# Revit family: 28L 2 to 6 units single sided indoor manifold system rev
name_source: partatom
category: Plumbing Fixtures
revit_build: Autodesk Revit 2017 (Build: 20160225_1515(x64)
units: mm (PartAtom-declared; Revit-internal decimal feet)

## family parameters
Always vertical = Yes
Cut with Voids When Loaded = No
Part Type = Normal
Room Calculation Point = No
Round Connector Dimension = Use Diameter
Shared = No
Work Plane-Based = No

## types (10) — shared parameters
Cold Water Inlet Pipe connector description = Male threaded connector R1-1/2"
Cold Water Inlet Pipe diameter = 38.1mm(DN 40)
Exhaust Air pipe connector description = 80-125mm coaxial air connector
Exhaust Air pipe connector system classification = Exhaust Air
Exhaust Air pipe diameter = 125.000 mm
Gas Inlet Pipe connector description = Male threaded connector R1-1/2"
Gas Inlet Pipe diameter = 38.1mm(DN 40)
Hot Water Outlet Pipe connector description = Male threaded connector R1-1/2"
Hot Water Outlet Pipe diameter = 38.1mm(DN 40)
Supply Air/Air Inlet connector classification = Supply Air
Supply Air/Air Inlet pipe connector description = 80-125mm coaxial air connector
Supply Air/Air Inlet pipe diameter = 80.000 mm

## per-type parameters (varying)
- 28L 2 units single sided indoor floor mounted: 2 Unit L=Yes; 2 Unit R=No; 3 Unit L=No; 3 Unit R=No; Array Offset=360.000 mm; Base Offset L=794.000 mm; Base Offset R=1040.000 mm; Base Support L=Yes; Base Support R=No; Connector Left=2324.000 mm; Connector Right=1550.000 mm; D1=1757.000 mm; D2=217.000 mm; D3=1757.000 mm; No of Connectors 1=2; No of Connectors 2=2; No. of power supply point required=2; Nominal depth=900mm; Nominal height=1540mm; Nominal width=794mm; Number of Gas Water Heaters=2; Product SKU Dux brand=D22800FN/LFx; Product SKU Thermann brand=T22800FN/LFx; Product description=Gas Water heater Manifold 2 unit indoor floor mounted; Total Max. power requirement=386W; Total nominal gas consumption (MJ/h)=410; Total number of exhaust air connections=2; Total number of supply air connections=2; Unit Offset=41.300 mm; Weight (Kg)=90
- 28L 3 units single sided indoor floor mounted: 2 Unit L=No; 2 Unit R=No; 3 Unit L=Yes; 3 Unit R=No; Array Offset=360.000 mm; Base Offset L=1170.000 mm; Base Offset R=1040.000 mm; Base Support L=Yes; Base Support R=No; Connector Left=2700.000 mm; Connector Right=1550.000 mm; D1=2125.000 mm; D2=225.000 mm; D3=1765.000 mm; No of Connectors 1=3; No of Connectors 2=3; No. of power supply point required=3; Nominal depth=900mm; Nominal height=1540mm; Nominal width=1170mm; Number of Gas Water Heaters=3; Product SKU Dux brand=D32800FN/LFx; Product SKU Thermann brand=T32800FN/LFx; Product description=Gas Water heater Manifold 3 unit indoor floor mounted; Total Max. power requirement=579W; Total nominal gas consumption (MJ/h)=615; Total number of exhaust air connections=3; Total number of supply air connections=3; Unit Offset=41.300 mm; Weight (Kg)=120
- 28L 4 units single sided indoor floor mounted: 2 Unit L=Yes; 2 Unit R=Yes; 3 Unit L=No; 3 Unit R=No; Array Offset=360.000 mm; Base Offset L=794.000 mm; Base Offset R=794.000 mm; Base Support L=Yes; Base Support R=Yes; Connector Left=2324.000 mm; Connector Right=756.000 mm; D1=963.000 mm; D2=217.000 mm; D3=963.000 mm; No of Connectors 1=2; No of Connectors 2=2; No. of power supply point required=4; Nominal depth=900mm; Nominal height=1540mm; Nominal width=1588mm; Number of Gas Water Heaters=4; Product SKU Dux brand=D42800FN/LFx; Product SKU Thermann brand=T42800FN/LFx; Product description=Gas Water heater Manifold 4 unit indoor floor mounted; Total Max. power requirement=772W; Total nominal gas consumption (MJ/h)=820; Total number of exhaust air connections=4; Total number of supply air connections=4; Unit Offset=41.300 mm; Weight (Kg)=180
- 28L 5 units single sided indoor floor mounted: 2 Unit L=No; 2 Unit R=Yes; 3 Unit L=Yes; 3 Unit R=No; Array Offset=360.000 mm; Base Offset L=1170.000 mm; Base Offset R=794.000 mm; Base Support L=Yes; Base Support R=Yes; Connector Left=2700.000 mm; Connector Right=756.000 mm; D1=2125.000 mm; D2=225.000 mm; D3=963.000 mm; No of Connectors 1=2; No of Connectors 2=3; No. of power supply point required=5; Nominal depth=900mm; Nominal height=1540mm; Nominal width=1964mm; Number of Gas Water Heaters=5; Product SKU Dux brand=D52800FN/LFx; Product SKU Thermann brand=T52800FN/LFx; Product description=Gas Water heater Manifold 5 unit indoor floor mounted; Total Max. power requirement=965W; Total nominal gas consumption (MJ/h)=1025; Total number of exhaust air connections=5; Total number of supply air connections=5; Unit Offset=41.300 mm; Weight (Kg)=210
- 28L 6 units single sided indoor floor mounted: 2 Unit L=No; 2 Unit R=No; 3 Unit L=Yes; 3 Unit R=Yes; Array Offset=1170.000 mm; Base Offset L=1170.000 mm; Base Offset R=1170.000 mm; Base Support L=Yes; Base Support R=Yes; Connector Left=2700.000 mm; Connector Right=380.000 mm; D1=1315.000 mm; D2=225.000 mm; D3=595.000 mm; No of Connectors 1=3; No of Connectors 2=3; No. of power supply point required=6; Nominal depth=900mm; Nominal height=1540mm; Nominal width=2340mm; Number of Gas Water Heaters=6; Product SKU Dux brand=D62800FN/LFx; Product SKU Thermann brand=T62800FN/LFx; Product description=Gas Water heater Manifold 6 unit  indoor floor mounted; Total Max. power requirement=1158W; Total nominal gas consumption (MJ/h)=1230; Total number of exhaust air connections=6; Total number of supply air connections=6; Unit Offset=41.300 mm; Weight (Kg)=240
- 28L 2 units single sided indoor wall mounted: 2 Unit L=Yes; 2 Unit R=No; 3 Unit L=No; 3 Unit R=No; Array Offset=360.000 mm; Base Offset L=1040.000 mm; Base Offset R=1040.000 mm; Base Support L=No; Base Support R=No; Connector Left=2324.000 mm; Connector Right=1550.000 mm; D1=1757.000 mm; D2=217.000 mm; D3=1757.000 mm; No of Connectors 1=2; No of Connectors 2=2; No. of power supply point required=2; Nominal depth=332mm; Nominal height=1500mm; Nominal width=794mm; Number of Gas Water Heaters=2; Product SKU Dux brand=D22800FN/LWx; Product SKU Thermann brand=T22800FN/LWx; Product description=Gas Water heater Manifold 2 unit indoor wall mounted; Total Max. power requirement=386W; Total nominal gas consumption (MJ/h)=410; Total number of exhaust air connections=2; Total number of supply air connections=2; Unit Offset=0.000 mm; Weight (Kg)=90
- 28L 3 units single sided indoor wall mounted: 2 Unit L=No; 2 Unit R=No; 3 Unit L=Yes; 3 Unit R=No; Array Offset=360.000 mm; Base Offset L=1540.000 mm; Base Offset R=1040.000 mm; Base Support L=No; Base Support R=No; Connector Left=2700.000 mm; Connector Right=1550.000 mm; D1=2125.000 mm; D2=225.000 mm; D3=1765.000 mm; No of Connectors 1=3; No of Connectors 2=3; No. of power supply point required=3; Nominal depth=332mm; Nominal height=1500mm; Nominal width=1170mm; Number of Gas Water Heaters=3; Product SKU Dux brand=D32800FN/LWx; Product SKU Thermann brand=T32800FN/LWx; Product description=Gas Water heater Manifold 3 unit indoor wall mounted; Total Max. power requirement=579W; Total nominal gas consumption (MJ/h)=615; Total number of exhaust air connections=3; Total number of supply air connections=3; Unit Offset=0.000 mm; Weight (Kg)=120
- 28L 4 units single sided indoor wall mounted: 2 Unit L=Yes; 2 Unit R=Yes; 3 Unit L=No; 3 Unit R=No; Array Offset=360.000 mm; Base Offset L=1040.000 mm; Base Offset R=1040.000 mm; Base Support L=No; Base Support R=No; Connector Left=2324.000 mm; Connector Right=756.000 mm; D1=963.000 mm; D2=217.000 mm; D3=963.000 mm; No of Connectors 1=2; No of Connectors 2=2; No. of power supply point required=4; Nominal depth=332mm; Nominal height=1500mm; Nominal width=1588mm; Number of Gas Water Heaters=4; Product SKU Dux brand=D42800FN/LWx; Product SKU Thermann brand=T42800FN/LWx; Product description=Gas Water heater Manifold 4 unit indoor wall mounted; Total Max. power requirement=772W; Total nominal gas consumption (MJ/h)=820; Total number of exhaust air connections=4; Total number of supply air connections=4; Unit Offset=0.000 mm; Weight (Kg)=180
- 28L 5 units single sided indoor wall mounted: 2 Unit L=No; 2 Unit R=Yes; 3 Unit L=Yes; 3 Unit R=No; Array Offset=360.000 mm; Base Offset L=1540.000 mm; Base Offset R=1040.000 mm; Base Support L=No; Base Support R=No; Connector Left=2700.000 mm; Connector Right=756.000 mm; D1=2125.000 mm; D2=225.000 mm; D3=963.000 mm; No of Connectors 1=2; No of Connectors 2=3; No. of power supply point required=5; Nominal depth=332mm; Nominal height=1500mm; Nominal width=1964mm; Number of Gas Water Heaters=5; Product SKU Dux brand=D52800FN/LWx; Product SKU Thermann brand=T52800FN/LWx; Product description=Gas Water heater Manifold 5 unit  indoor wall mounted; Total Max. power requirement=965W; Total nominal gas consumption (MJ/h)=1025; Total number of exhaust air connections=5; Total number of supply air connections=5; Unit Offset=0.000 mm; Weight (Kg)=210
- 28L 6 units single sided indoor wall mounted: 2 Unit L=No; 2 Unit R=No; 3 Unit L=Yes; 3 Unit R=Yes; Array Offset=1170.000 mm; Base Offset L=1040.000 mm; Base Offset R=1040.000 mm; Base Support L=No; Base Support R=No; Connector Left=2700.000 mm; Connector Right=380.000 mm; D1=1315.000 mm; D2=225.000 mm; D3=595.000 mm; No of Connectors 1=3; No of Connectors 2=3; No. of power supply point required=6; Nominal depth=332mm; Nominal height=1500mm; Nominal width=2340mm; Number of Gas Water Heaters=6; Product SKU Dux brand=D62800FN/LWx; Product SKU Thermann brand=T62800FN/LWx; Product description=Gas Water heater Manifold 6 unit indoor wall mounted; Total Max. power requirement=1158W; Total nominal gas consumption (MJ/h)=1230; Total number of exhaust air connections=6; Total number of supply air connections=6; Unit Offset=0.000 mm; Weight (Kg)=240

## geometry (parser evidence)
native form markers: Sweep x13
no freeform markers — native parametric forms only
